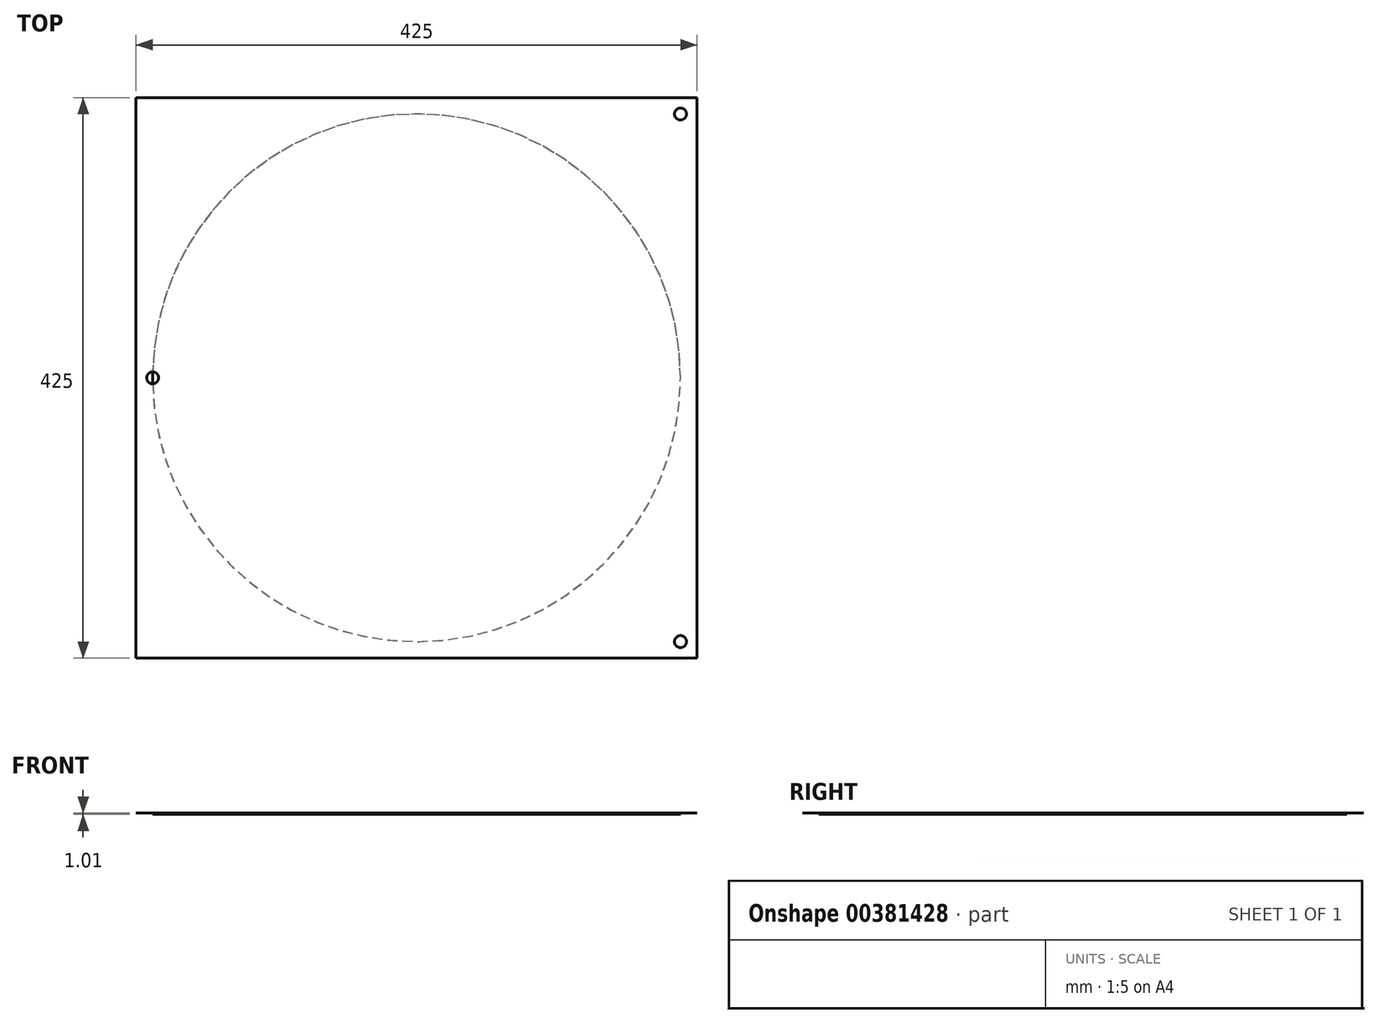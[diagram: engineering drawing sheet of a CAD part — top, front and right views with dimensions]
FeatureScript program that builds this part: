
annotation { "Feature Type Name" : "Feature", "Feature Type Description" : "" }
export const myFeature = defineFeature(function(context is Context, id is Id, definition is map)
    precondition{}
    {
        {
            var Q0;
            Q0=qCreatedBy(makeId("Top.planeOp"),FACE);
            var sketch = newSketch(context, id + "F0", { "sketchPlane" : qUnion([Q0])});
            skLineSegment(sketch, "E0.bottom", {"start": v(212.5, -212.5) * mm, "end": v(-212.5, -212.5) * mm});
            skLineSegment(sketch, "E0.top", {"start": v(212.5, 212.5) * mm, "end": v(-212.5, 212.5) * mm});
            skLineSegment(sketch, "E0.left", {"start": v(212.5, -212.5) * mm, "end": v(212.5, 212.5) * mm});
            skLineSegment(sketch, "E0.right", {"start": v(-212.5, -212.5) * mm, "end": v(-212.5, 212.5) * mm});
            skPoint(sketch, "E0.middle", {"position": v(0, 0) * mm});
            skSolve(sketch);
        }
        {
            var Q0;
            Q0 = qSketchRegion(id + "F0", true);
            extrude(context, id + "F1", {"entities" : qUnion([Q0]), "oppositeDirection" : true, "depth" : 3 / 203.2 * mm});
        }
        {
            var Q0;
            Q0=makeQuery(id+"F1.opExtrude","CAP_FACE",FACE,{"disambiguationData":[OSD([sQuery(id+"F0.wireOp",EDGE,"E0.bottom"),sQuery(id+"F0.wireOp",EDGE,"E0.top"),sQuery(id+"F0.wireOp",EDGE,"E0.left"),sQuery(id+"F0.wireOp",EDGE,"E0.right")])],"isStart":false});
            var sketch = newSketch(context, id + "F2", { "sketchPlane" : qUnion([Q0])});
            skCircle(sketch, "E1", {"center": v(0, 0) * mm, "radius": 200 * mm});
            skSolve(sketch);
        }
        {
            var Q0;
            Q0 = qSketchRegion(id + "F2", true);
            extrude(context, id + "F3", {"entities" : qUnion([Q0]), "depth" : 1 * mm});
        }
        {
            var Q0;
            Q0=makeQuery(id+"F1.opExtrude","CAP_FACE",FACE,{"disambiguationData":[OSD([sQuery(id+"F0.wireOp",EDGE,"E0.bottom"),sQuery(id+"F0.wireOp",EDGE,"E0.top"),sQuery(id+"F0.wireOp",EDGE,"E0.left"),sQuery(id+"F0.wireOp",EDGE,"E0.right")])],"isStart":true});
            var sketch = newSketch(context, id + "F4", { "sketchPlane" : qUnion([Q0])});
            skLineSegment(sketch, "E2.bottom", {"start": v(-200, 200) * mm, "end": v(200, 200) * mm, "construction": true});
            skLineSegment(sketch, "E2.top", {"start": v(-200, -200) * mm, "end": v(200, -200) * mm, "construction": true});
            skLineSegment(sketch, "E2.left", {"start": v(-200, 200) * mm, "end": v(-200, -200) * mm, "construction": true});
            skLineSegment(sketch, "E2.right", {"start": v(200, 200) * mm, "end": v(200, -200) * mm, "construction": true});
            skPoint(sketch, "E2.middle", {"position": v(0, 0) * mm});
            skPoint(sketch, "E3", {"position": v(-200, 0) * mm});
            skSolve(sketch);
        }
        {
            var Q0;
            Q0=sQuery(id+"F4.wireOp",VERTEX,"E2.right.end");
            var Q1;
            Q1=sQuery(id+"F4.wireOp",VERTEX,"E2.right.start");
            var Q2;
            Q2=sQuery(id+"F4.wireOp",VERTEX,"E3");
            var Q3;
            Q3=makeQuery(id+"F1.opExtrude","SWEPT_BODY",BODY,{"disambiguationData":[OSD([sQuery(id+"F0.wireOp",EDGE,"E0.bottom"),sQuery(id+"F0.wireOp",EDGE,"E0.top"),sQuery(id+"F0.wireOp",EDGE,"E0.left"),sQuery(id+"F0.wireOp",EDGE,"E0.right")])]});
            hole(context, id + "F5", {"style" : HoleStyle.C_SINK, "endStyle" : HoleEndStyle.THROUGH, "standardTappedOrClearance" : lookupTablePath({ "standard" : "ANSI", "fit" : "Close", "size" : "#8", "type" : "Clearance" }), "standardBlindInLast" : lookupTablePath({ "fit" : "Close", "standard" : "ANSI", "size" : "#8", "type" : "Clearance" }), "holeDiameter" : 4.32 * mm, "cSinkDiameter" : 9.12 * mm, "cSinkAngle" : 82 * degree, "isTappedThrough" : true, "tappedDepth" : 12 * mm, "tapClearance" : 3, "locations" : qUnion([Q0, Q1, Q2]), "scope" : qUnion([Q3])});
        }
    });
